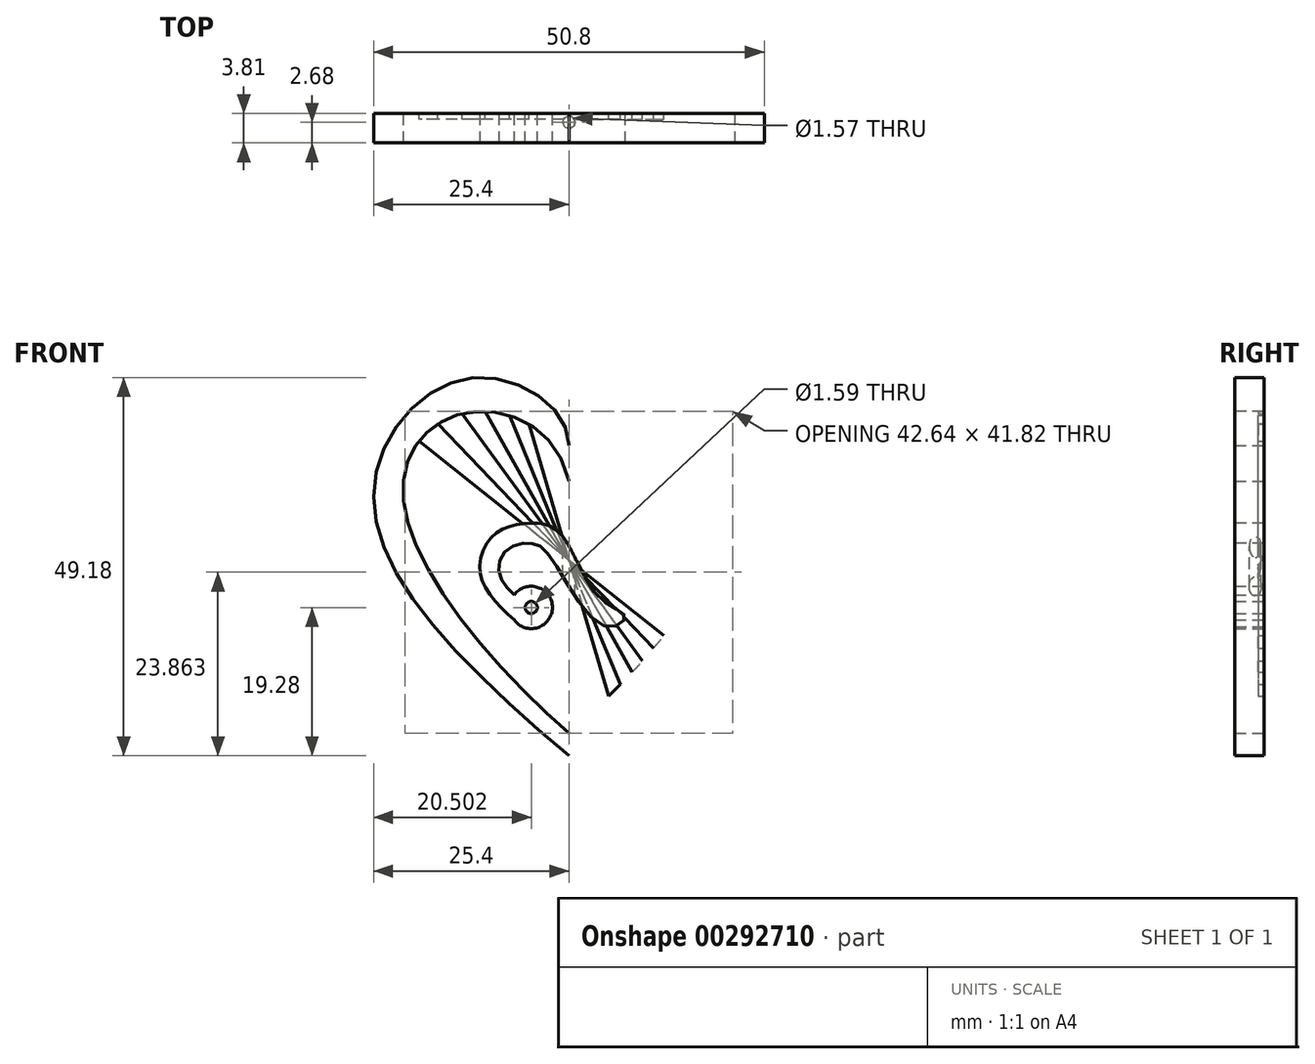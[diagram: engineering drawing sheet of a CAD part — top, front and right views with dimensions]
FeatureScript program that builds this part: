
annotation { "Feature Type Name" : "Feature", "Feature Type Description" : "" }
export const myFeature = defineFeature(function(context is Context, id is Id, definition is map)
    precondition{}
    {
        {
            var Q0;
            Q0=qCreatedBy(makeId("Front.planeOp"),FACE);
            var sketch = newSketch(context, id + "F0", { "sketchPlane" : qUnion([Q0])});
            skFitSpline(sketch, "E0", {"points": [v(0, -25.43) * mm, v(-25.4, 8.42) * mm, v(-12.64, 23.69) * mm, v(0, 14.9) * mm], "startDerivative": vector(-91.97, 78) * mm, "endDerivative": vector(0, -58.35) * mm});
            skFitSpline(sketch, "E1", {"points": [v(0, 10.3) * mm, v(13.91, 19.05) * mm, v(21.57, 8.26) * mm, v(0, -22.48) * mm], "startDerivative": vector(15.93, 75.73) * mm, "endDerivative": vector(-67.5, -58.85) * mm});
            skFitSpline(sketch, "E2.MirrorCS", {"points": [v(0, 10.3) * mm, v(-13.91, 19.05) * mm, v(-21.57, 8.26) * mm, v(0, -22.48) * mm], "startDerivative": vector(-15.93, 75.73) * mm, "endDerivative": vector(67.5, -58.85) * mm});
            skFitSpline(sketch, "E3.MirrorCS", {"points": [v(0, -25.43) * mm, v(25.4, 8.42) * mm, v(12.64, 23.69) * mm, v(0, 14.9) * mm], "startDerivative": vector(91.97, 78) * mm, "endDerivative": vector(0, -58.35) * mm});
            skSolve(sketch);
        }
        {
            var Q0;
            Q0=qCreatedBy(makeId("Front.planeOp"),FACE);
            var sketch = newSketch(context, id + "F1", { "sketchPlane" : qUnion([Q0])});
            skCircle(sketch, "E4", {"center": v(-4.9, -6.15) * mm, "radius": 0.8 * mm});
            skArc(sketch, "E5", {"start": v(-4.9, -3.4) * mm, "mid": v(-2.45, -7.4) * mm, "end": v(-7.12, -7.77) * mm});
            skArc(sketch, "E6", {"start": v(-4.9, -3.4) * mm, "mid": v(-6.13, -3.7) * mm, "end": v(-7.1, -4.5) * mm});
            skPoint(sketch, "E7.6.internal.snap0", {"position": v(-2.45, -7.4) * mm});
            skPoint(sketch, "E7.8.internal.snap0", {"position": v(-2.45, -7.4) * mm});
            skFitSpline(sketch, "E7", {"points": [v(-7.12, -7.77) * mm, v(-11.42, -2.15) * mm, v(-9.95, 3.14) * mm, v(-5, 4.83) * mm, v(-1.04, 3.35) * mm, v(4.16, -5.06) * mm, v(7.28, -7.4) * mm, v(4.77, -8.63) * mm, v(-2.45, 0.48) * mm, v(-4.99, 2.2) * mm, v(-8.27, 1.21) * mm, v(-9, -1.94) * mm, v(-7.1, -4.5) * mm], "startDerivative": vector(-56.7, 52.39) * mm, "endDerivative": vector(36.05, -34.12) * mm});
            skFitSpline(sketch, "E8", {"points": [v(-1.04, 3.35) * mm, v(-1.04, 5.52) * mm, v(0, 6.24) * mm, v(1.52, 6.03) * mm, v(4.05, 4.43) * mm, v(7.67, 4.28) * mm, v(12.06, 10.01) * mm, v(15.42, 8.87) * mm, v(14.02, 8.46) * mm, v(10.82, 3.35) * mm, v(7.82, 1.38) * mm, v(4.57, 1.54) * mm, v(2.86, 2.73) * mm, v(1.16, 2.67) * mm, v(0.96, 0) * mm], "startDerivative": vector(-6.08, 39.76) * mm, "endDerivative": vector(6, -48.25) * mm});
            skLineSegment(sketch, "E9", {"start": v(0.96, 0) * mm, "end": v(0.96, 0) * mm});
            skFitSpline(sketch, "E10", {"points": [v(-7.12, -7.77) * mm, v(-11.42, -2.15) * mm, v(-9.95, 3.14) * mm, v(-5, 4.83) * mm, v(-1.04, 3.35) * mm, v(4.16, -5.06) * mm, v(7.28, -7.4) * mm, v(4.77, -8.63) * mm, v(-2.45, 0.48) * mm, v(-4.99, 2.2) * mm, v(-8.27, 1.21) * mm, v(-9, -1.94) * mm, v(-7.1, -4.5) * mm], "startDerivative": vector(-56.7, 52.39) * mm, "endDerivative": vector(36.05, -34.12) * mm});
            skSolve(sketch);
        }
        {
            var Q0;
            Q0=makeQuery(id+"F1.imprint","IMPRINT",FACE,{"disambiguationData":[TD([[makeQuery(id+"F1.imprint","IMPRINT",EDGE,{"derivedFrom":sQuery(id+"F1.wireOp",EDGE,"E4")}),-1.0]])]});
            var Q1;
            Q1=sQuery(id+"F1.wireOp",EDGE,"E8");
            var Q2;
            Q2=sQuery(id+"F1.wireOp",EDGE,"E10");
            var Q3;
            Q3=sQuery(id+"F1.wireOp",EDGE,"E5");
            var Q4;
            Q4=sQuery(id+"F1.wireOp",EDGE,"E6");
            var Q5;
            Q5=sQuery(id+"F1.wireOp",EDGE,"E7");
            var Q6;
            Q6=sQuery(id+"F1.wireOp",EDGE,"E4");
            extrude(context, id + "F2", {"entities" : qUnion([Q0]), "surfaceEntities" : qUnion([Q1, Q2, Q3, Q4, Q5, Q6]), "depth" : 3.8 * mm});
        }
        {
            var Q0;
            {var subQ0=sQuery(id+"F0.wireOp",EDGE,"E0");Q0=makeQuery(id+"F0.imprint","IMPRINT",FACE,{"disambiguationData":[TD([[makeQuery(id+"F0.imprint","IMPRINT",EDGE,{"derivedFrom":subQ0}),-1.0]])]});}
            extrude(context, id + "F3", {"entities" : qUnion([Q0]), "depth" : 3.8 * mm});
        }
        {
            var Q0;
            Q0=qCreatedBy(makeId("Front.planeOp"),FACE);
            var sketch = newSketch(context, id + "F4", { "sketchPlane" : qUnion([Q0])});
            skLineSegment(sketch, "E11", {"start": v(0, 0) * mm, "end": v(-5.16, 17.69) * mm});
            skLineSegment(sketch, "E12", {"start": v(0, 0) * mm, "end": v(-7.72, 18.81) * mm});
            skLineSegment(sketch, "E13", {"start": v(0, 0) * mm, "end": v(-10.91, 19.34) * mm});
            skLineSegment(sketch, "E14", {"start": v(0, 0) * mm, "end": v(-13.89, 19.05) * mm});
            skLineSegment(sketch, "E15", {"start": v(0, 0) * mm, "end": v(-17.05, 17.73) * mm});
            skLineSegment(sketch, "E16", {"start": v(0, 0) * mm, "end": v(-19.49, 15.5) * mm});
            skArc(sketch, "E17", {"start": v(-5.16, 17.69) * mm, "mid": v(-6.4, 18.33) * mm, "end": v(-7.72, 18.81) * mm});
            skArc(sketch, "E18", {"start": v(-10.91, 19.34) * mm, "mid": v(-12.41, 19.34) * mm, "end": v(-13.89, 19.05) * mm});
            skArc(sketch, "E19", {"start": v(-17.05, 17.73) * mm, "mid": v(-18.37, 16.74) * mm, "end": v(-19.49, 15.5) * mm});
            skArc(sketch, "E20.MirrorCS", {"start": v(-21.1, 12.63) * mm, "mid": v(-20.43, 14.15) * mm, "end": v(-19.49, 15.5) * mm});
            skLineSegment(sketch, "E21", {"start": v(0, 36.15) * mm, "end": v(0, -31.52) * mm});
            skLineSegment(sketch, "E22.MirrorCS", {"start": v(0, 0) * mm, "end": v(5.16, -17.69) * mm});
            skLineSegment(sketch, "E23.MirrorCS", {"start": v(0, 0) * mm, "end": v(6.67, -16.16) * mm});
            skLineSegment(sketch, "E24.MirrorCS", {"start": v(0, 0) * mm, "end": v(8.2, -14.54) * mm});
            skLineSegment(sketch, "E25.MirrorCS", {"start": v(0, 0) * mm, "end": v(9.55, -13.08) * mm});
            skLineSegment(sketch, "E26.MirrorCS", {"start": v(0, 0) * mm, "end": v(11, -11.42) * mm});
            skLineSegment(sketch, "E27.MirrorCS", {"start": v(0, 0) * mm, "end": v(12.33, -9.82) * mm});
            skArc(sketch, "E28", {"start": v(6.67, -16.16) * mm, "mid": v(5.9, -16.92) * mm, "end": v(5.16, -17.69) * mm});
            skArc(sketch, "E29", {"start": v(8.2, -14.54) * mm, "mid": v(8.9, -13.84) * mm, "end": v(9.55, -13.08) * mm});
            skArc(sketch, "E30", {"start": v(11, -11.42) * mm, "mid": v(11.69, -10.63) * mm, "end": v(12.33, -9.82) * mm});
            skSolve(sketch);
        }
        {
            var Q0;
            Q0=makeQuery(id+"F4.imprint","IMPRINT",FACE,{"disambiguationData":[TD([[makeQuery(id+"F4.imprint","IMPRINT",EDGE,{"derivedFrom":sQuery(id+"F4.wireOp",EDGE,"E15")}),1.0]])]});
            var Q1;
            Q1=makeQuery(id+"F4.imprint","IMPRINT",FACE,{"disambiguationData":[TD([[makeQuery(id+"F4.imprint","IMPRINT",EDGE,{"derivedFrom":sQuery(id+"F4.wireOp",EDGE,"E13")}),1.0]])]});
            var Q2;
            Q2=makeQuery(id+"F4.imprint","IMPRINT",FACE,{"disambiguationData":[TD([[makeQuery(id+"F4.imprint","IMPRINT",EDGE,{"derivedFrom":sQuery(id+"F4.wireOp",EDGE,"E11")}),1.0]])]});
            var Q3;
            Q3=makeQuery(id+"F4.imprint","IMPRINT",FACE,{"disambiguationData":[TD([[makeQuery(id+"F4.imprint","IMPRINT",EDGE,{"derivedFrom":sQuery(id+"F4.wireOp",EDGE,"E22.MirrorCS")}),1.0]])]});
            var Q4;
            Q4=makeQuery(id+"F4.imprint","IMPRINT",FACE,{"disambiguationData":[TD([[makeQuery(id+"F4.imprint","IMPRINT",EDGE,{"derivedFrom":sQuery(id+"F4.wireOp",EDGE,"E24.MirrorCS")}),1.0]])]});
            var Q5;
            Q5=makeQuery(id+"F4.imprint","IMPRINT",FACE,{"disambiguationData":[TD([[makeQuery(id+"F4.imprint","IMPRINT",EDGE,{"derivedFrom":sQuery(id+"F4.wireOp",EDGE,"E26.MirrorCS")}),1.0]])]});
            extrude(context, id + "F5", {"entities" : qUnion([Q0, Q1, Q2, Q3, Q4, Q5]), "depth" : 0.76 * mm});
        }
        {
            var Q0;
            Q0=qCreatedBy(makeId("Top.planeOp"),FACE);
            cPlane(context, id + "F6", {"entities" : qUnion([Q0]), "cplaneType" : CPlaneType.OFFSET, "offset" : 6.8 * mm, "width" : 152.4 * mm, "height" : 152.4 * mm});
        }
        {
            var Q0;
            Q0=qCreatedBy(id+"F6.planeOp",FACE);
            var sketch = newSketch(context, id + "F7", { "sketchPlane" : qUnion([Q0])});
            skCircle(sketch, "E31", {"center": v(0, -1.13) * mm, "radius": 0.79 * mm});
            skSolve(sketch);
        }
        {
            var Q0;
            Q0=makeQuery(id+"F7.imprint","IMPRINT",FACE,{"disambiguationData":[TD([[makeQuery(id+"F7.imprint","IMPRINT",EDGE,{"derivedFrom":sQuery(id+"F7.wireOp",EDGE,"E31")}),1.0]])]});
            var Q1;
            Q1=sQuery(id+"F7.wireOp",EDGE,"E31");
            extrude(context, id + "F8", {"entities" : qUnion([Q0]), "operationType" : NewBodyOperationType.REMOVE, "surfaceEntities" : qUnion([Q1]), "oppositeDirection" : true, "depth" : 12.7 * mm});
        }
    });
